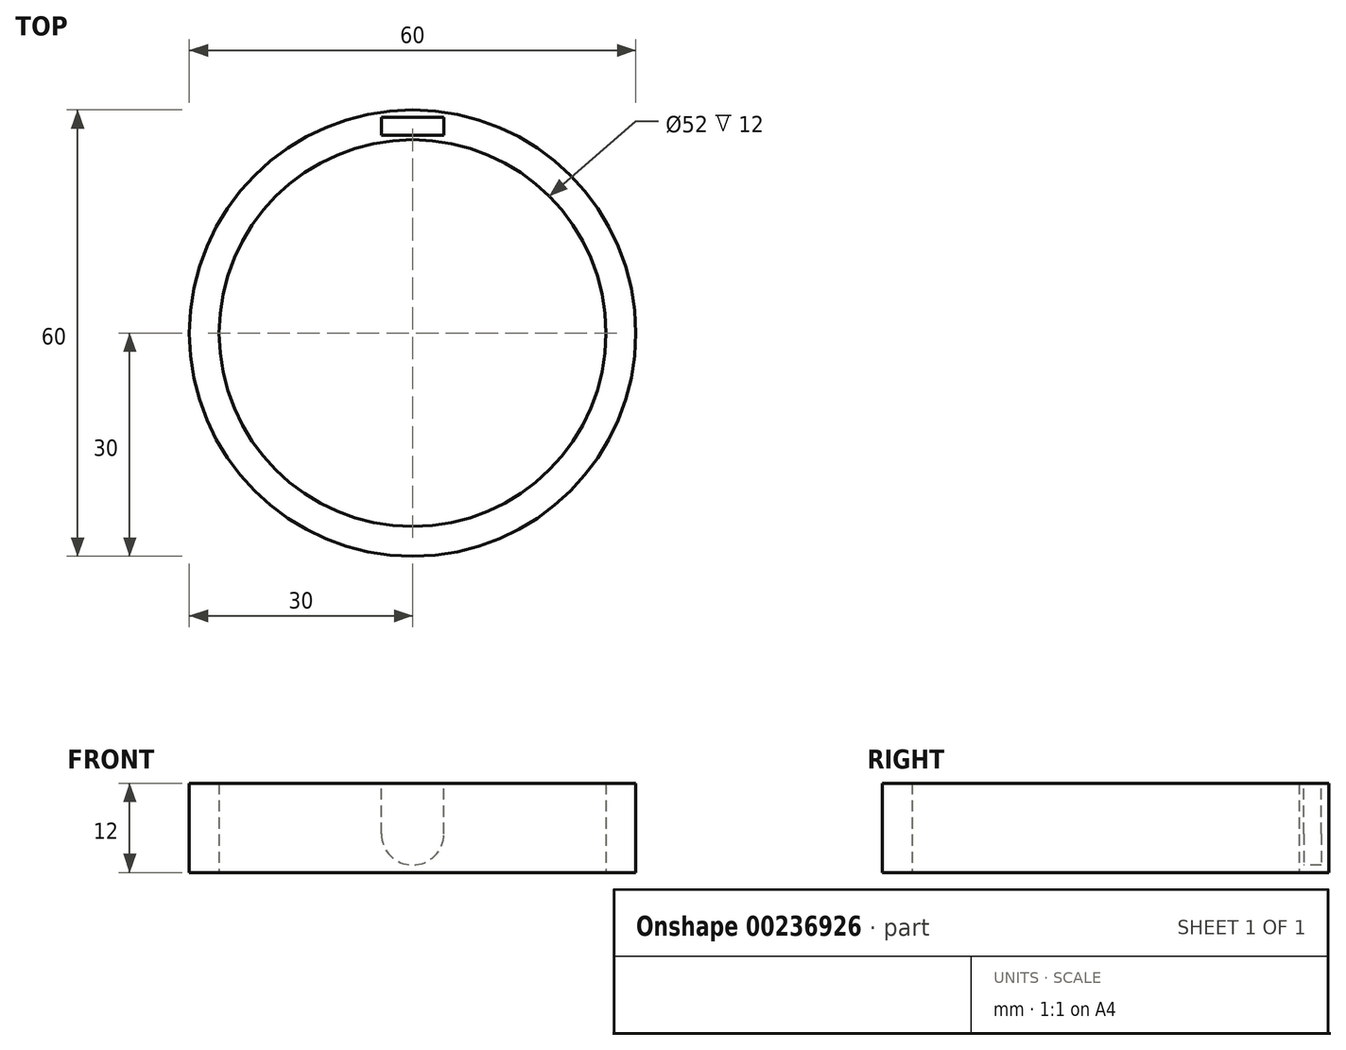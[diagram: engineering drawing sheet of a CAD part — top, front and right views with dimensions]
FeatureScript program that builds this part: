
annotation { "Feature Type Name" : "Feature", "Feature Type Description" : "" }
export const myFeature = defineFeature(function(context is Context, id is Id, definition is map)
    precondition{}
    {
        {
            var Q0;
            Q0=qCreatedBy(makeId("Top.planeOp"),FACE);
            var sketch = newSketch(context, id + "F0", { "sketchPlane" : qUnion([Q0])});
            skCircle(sketch, "E0", {"center": v(0, 0) * mm, "radius": 30 * mm});
            skCircle(sketch, "E1", {"center": v(0, 0) * mm, "radius": 26 * mm});
            skSolve(sketch);
        }
        {
            var Q0;
            Q0 = qSketchRegion(id + "F0", true);
            extrude(context, id + "F1", {"entities" : qUnion([Q0]), "depth" : 12 * mm});
        }
        {
            var Q0;
            Q0=makeQuery(id+"F1.opExtrude","CAP_FACE",FACE,{"disambiguationData":[OSD([sQuery(id+"F0.wireOp",EDGE,"E0"),sQuery(id+"F0.wireOp",EDGE,"E1")])],"isStart":false});
            var sketch = newSketch(context, id + "F2", { "sketchPlane" : qUnion([Q0])});
            skLineSegment(sketch, "E2.bottom", {"start": v(4.2, 26.6) * mm, "end": v(-4.2, 26.6) * mm});
            skLineSegment(sketch, "E2.top", {"start": v(4.2, 29) * mm, "end": v(-4.2, 29) * mm});
            skLineSegment(sketch, "E2.left", {"start": v(4.2, 26.6) * mm, "end": v(4.2, 29) * mm});
            skLineSegment(sketch, "E2.right", {"start": v(-4.2, 26.6) * mm, "end": v(-4.2, 29) * mm});
            skPoint(sketch, "E2.middle", {"position": v(0, 27.8) * mm});
            skSolve(sketch);
        }
        {
            var Q0;
            Q0 = qSketchRegion(id + "F2", true);
            extrude(context, id + "F3", {"entities" : qUnion([Q0]), "operationType" : NewBodyOperationType.REMOVE, "oppositeDirection" : true, "depth" : 11 * mm});
        }
        {
            var Q0;
            Q0=makeQuery(id+"F3.boolean.opBoolean","COPY",EDGE,{"derivedFrom":makeQuery(id+"F3.opExtrude","CAP_EDGE",EDGE,{"disambiguationData":[OSD([sQuery(id+"F2.wireOp",EDGE,"E2.right")])],"isStart":false})});
            var Q1;
            Q1=makeQuery(id+"F3.boolean.opBoolean","COPY",EDGE,{"derivedFrom":makeQuery(id+"F3.opExtrude","CAP_EDGE",EDGE,{"disambiguationData":[OSD([sQuery(id+"F2.wireOp",EDGE,"E2.left")])],"isStart":false})});
            fillet(context, id + "F4", {"entities" : qUnion([Q0, Q1]), "radius" : 4.2 * mm, "tangentPropagation" : true, "allowEdgeOverflow" : false});
        }
    });
